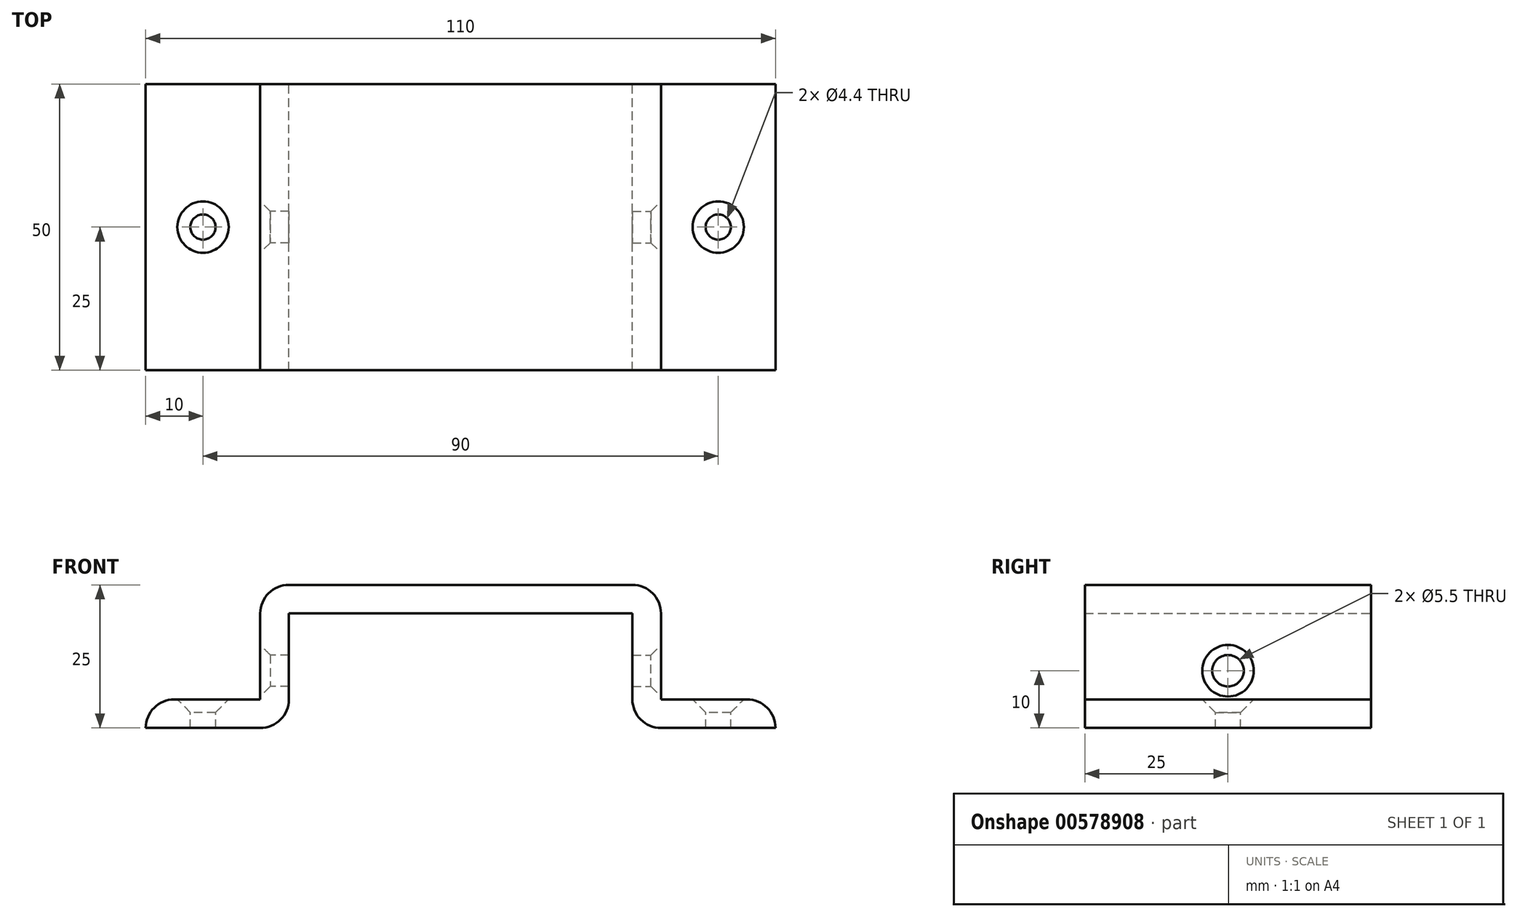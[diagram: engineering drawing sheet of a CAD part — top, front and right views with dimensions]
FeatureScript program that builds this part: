
annotation { "Feature Type Name" : "Feature", "Feature Type Description" : "" }
export const myFeature = defineFeature(function(context is Context, id is Id, definition is map)
    precondition{}
    {
        {
            var Q0;
            Q0=qCreatedBy(makeId("Front.planeOp"),FACE);
            var sketch = newSketch(context, id + "F0", { "sketchPlane" : qUnion([Q0])});
            skLineSegment(sketch, "E0", {"start": v(-55, 0) * mm, "end": v(-30, 0) * mm});
            skLineSegment(sketch, "E1", {"start": v(-30, 0) * mm, "end": v(-30, 20) * mm});
            skLineSegment(sketch, "E2", {"start": v(-30, 20) * mm, "end": v(30, 20) * mm});
            skLineSegment(sketch, "E3", {"start": v(30, 20) * mm, "end": v(30, 0) * mm});
            skLineSegment(sketch, "E4", {"start": v(30, 0) * mm, "end": v(55, 0) * mm});
            skLineSegment(sketch, "E5", {"start": v(-55, 0) * mm, "end": v(-55, 5) * mm});
            skLineSegment(sketch, "E6", {"start": v(-55, 5) * mm, "end": v(-35, 5) * mm});
            skLineSegment(sketch, "E7", {"start": v(-35, 5) * mm, "end": v(-35, 25) * mm});
            skLineSegment(sketch, "E8", {"start": v(-35, 25) * mm, "end": v(35, 25) * mm});
            skLineSegment(sketch, "E9", {"start": v(35, 25) * mm, "end": v(35, 5) * mm});
            skLineSegment(sketch, "E10", {"start": v(35, 5) * mm, "end": v(55, 5) * mm});
            skLineSegment(sketch, "E11", {"start": v(55, 5) * mm, "end": v(55, 0) * mm});
            skLineSegment(sketch, "E12", {"start": v(-30, 0) * mm, "end": v(30, 0) * mm, "construction": true});
            skSolve(sketch);
        }
        {
            var Q0;
            Q0=makeQuery(id+"F0.imprint","IMPRINT",FACE,{"disambiguationData":[TD([[makeQuery(id+"F0.imprint","IMPRINT",EDGE,{"derivedFrom":sQuery(id+"F0.wireOp",EDGE,"E0")}),1.0]])]});
            extrude(context, id + "F1", {"entities" : qUnion([Q0]), "depth" : 50 * mm, "offsetDistance" : 25 * mm});
        }
        {
            var Q0;
            Q0=makeQuery(id+"F1.opExtrude","SWEPT_FACE",FACE,{"disambiguationData":[OSD([sQuery(id+"F0.wireOp",EDGE,"E6")])]});
            var sketch = newSketch(context, id + "F2", { "sketchPlane" : qUnion([Q0])});
            skPoint(sketch, "E13", {"position": v(-45, -25) * mm});
            skLineSegment(sketch, "E14", {"start": v(-35, -25) * mm, "end": v(-55, -25) * mm, "construction": true});
            skLineSegment(sketch, "E15", {"start": v(-45, 0) * mm, "end": v(-45, -50) * mm, "construction": true});
            skSolve(sketch);
        }
        {
            var Q0;
            Q0=makeQuery(id+"F1.opExtrude","SWEPT_FACE",FACE,{"disambiguationData":[OSD([sQuery(id+"F0.wireOp",EDGE,"E10")])]});
            var sketch = newSketch(context, id + "F3", { "sketchPlane" : qUnion([Q0])});
            skLineSegment(sketch, "E16", {"start": v(45, 0) * mm, "end": v(45, -50) * mm, "construction": true});
            skLineSegment(sketch, "E17", {"start": v(55, -25) * mm, "end": v(35, -25) * mm, "construction": true});
            skPoint(sketch, "E18", {"position": v(45, -25) * mm});
            skSolve(sketch);
        }
        {
            var Q0;
            Q0=sQuery(id+"F2.wireOp",VERTEX,"E13");
            var Q1;
            Q1=sQuery(id+"F3.wireOp",VERTEX,"E18");
            var Q2;
            Q2=makeQuery(id+"F1.opExtrude","SWEPT_BODY",BODY,{"disambiguationData":[OSD([sQuery(id+"F0.wireOp",EDGE,"E0"),sQuery(id+"F0.wireOp",EDGE,"E1"),sQuery(id+"F0.wireOp",EDGE,"E2"),sQuery(id+"F0.wireOp",EDGE,"E3"),sQuery(id+"F0.wireOp",EDGE,"E4"),sQuery(id+"F0.wireOp",EDGE,"E5"),sQuery(id+"F0.wireOp",EDGE,"E6"),sQuery(id+"F0.wireOp",EDGE,"E7"),sQuery(id+"F0.wireOp",EDGE,"E8"),sQuery(id+"F0.wireOp",EDGE,"E9"),sQuery(id+"F0.wireOp",EDGE,"E10"),sQuery(id+"F0.wireOp",EDGE,"E11")])]});
            hole(context, id + "F4", {"style" : HoleStyle.C_SINK, "endStyle" : HoleEndStyle.THROUGH, "standardTappedOrClearance" : lookupTablePath({ "standard" : "ISO", "fit" : "Normal", "size" : "M4", "type" : "Clearance" }), "standardBlindInLast" : lookupTablePath({ "fit" : "Standard", "standard" : "ISO", "size" : "M4", "type" : "Clearance" }), "holeDiameter" : 4.4 * mm, "cSinkDiameter" : 8.96 * mm, "cSinkAngle" : 90 * degree, "isTappedThrough" : true, "tappedDepth" : 12 * mm, "tapClearance" : 3, "locations" : qUnion([Q0, Q1]), "scope" : qUnion([Q2]), "majorDiameter" : 5 * mm});
        }
        {
            var Q0;
            Q0=makeQuery(id+"F1.opExtrude","SWEPT_FACE",FACE,{"disambiguationData":[OSD([sQuery(id+"F0.wireOp",EDGE,"E7")])]});
            var sketch = newSketch(context, id + "F5", { "sketchPlane" : qUnion([Q0])});
            skPoint(sketch, "E19", {"position": v(25, 10) * mm});
            skLineSegment(sketch, "E20", {"start": v(25, 5) * mm, "end": v(25, 25) * mm, "construction": true});
            skSolve(sketch);
        }
        {
            var Q0;
            Q0=sQuery(id+"F5.wireOp",VERTEX,"E19");
            var Q1;
            Q1=makeQuery(id+"F1.opExtrude","SWEPT_BODY",BODY,{"disambiguationData":[OSD([sQuery(id+"F0.wireOp",EDGE,"E0"),sQuery(id+"F0.wireOp",EDGE,"E1"),sQuery(id+"F0.wireOp",EDGE,"E2"),sQuery(id+"F0.wireOp",EDGE,"E3"),sQuery(id+"F0.wireOp",EDGE,"E4"),sQuery(id+"F0.wireOp",EDGE,"E5"),sQuery(id+"F0.wireOp",EDGE,"E6"),sQuery(id+"F0.wireOp",EDGE,"E7"),sQuery(id+"F0.wireOp",EDGE,"E8"),sQuery(id+"F0.wireOp",EDGE,"E9"),sQuery(id+"F0.wireOp",EDGE,"E10"),sQuery(id+"F0.wireOp",EDGE,"E11")])]});
            hole(context, id + "F6", {"style" : HoleStyle.C_SINK, "endStyle" : HoleEndStyle.BLIND, "holeDiameter" : 5.5 * mm, "cSinkDiameter" : 9 * mm, "cSinkAngle" : 90 * degree, "majorDiameter" : 5 * mm, "holeDepth" : 5 * mm, "isTappedThrough" : true, "tappedDepth" : 12 * mm, "tapClearance" : 3, "locations" : qUnion([Q0]), "scope" : qUnion([Q1])});
        }
        {
            var Q0;
            Q0=makeQuery(id+"F1.opExtrude","SWEPT_FACE",FACE,{"disambiguationData":[OSD([sQuery(id+"F0.wireOp",EDGE,"E9")])]});
            var sketch = newSketch(context, id + "F7", { "sketchPlane" : qUnion([Q0])});
            skPoint(sketch, "E21", {"position": v(-25, 10) * mm});
            skLineSegment(sketch, "E22", {"start": v(-25, 5) * mm, "end": v(-25, 25) * mm, "construction": true});
            skSolve(sketch);
        }
        {
            var Q0;
            Q0=sQuery(id+"F7.wireOp",VERTEX,"E21");
            var Q1;
            Q1=makeQuery(id+"F1.opExtrude","SWEPT_BODY",BODY,{"disambiguationData":[OSD([sQuery(id+"F0.wireOp",EDGE,"E0"),sQuery(id+"F0.wireOp",EDGE,"E1"),sQuery(id+"F0.wireOp",EDGE,"E2"),sQuery(id+"F0.wireOp",EDGE,"E3"),sQuery(id+"F0.wireOp",EDGE,"E4"),sQuery(id+"F0.wireOp",EDGE,"E5"),sQuery(id+"F0.wireOp",EDGE,"E6"),sQuery(id+"F0.wireOp",EDGE,"E7"),sQuery(id+"F0.wireOp",EDGE,"E8"),sQuery(id+"F0.wireOp",EDGE,"E9"),sQuery(id+"F0.wireOp",EDGE,"E10"),sQuery(id+"F0.wireOp",EDGE,"E11")])]});
            hole(context, id + "F8", {"style" : HoleStyle.C_SINK, "endStyle" : HoleEndStyle.BLIND, "holeDiameter" : 5.5 * mm, "cSinkDiameter" : 9 * mm, "cSinkAngle" : 90 * degree, "majorDiameter" : 5 * mm, "holeDepth" : 5 * mm, "isTappedThrough" : true, "tappedDepth" : 12 * mm, "tapClearance" : 3, "locations" : qUnion([Q0]), "scope" : qUnion([Q1])});
        }
        {
            var Q0;
            Q0=makeQuery(id+"F1.opExtrude","SWEPT_EDGE",EDGE,{"disambiguationData":[OSD([sQuery(id+"F0.wireOp",EDGE,"E0"),sQuery(id+"F0.wireOp",EDGE,"E1")])]});
            var Q1;
            Q1=makeQuery(id+"F1.opExtrude","SWEPT_EDGE",EDGE,{"disambiguationData":[OSD([sQuery(id+"F0.wireOp",EDGE,"E3"),sQuery(id+"F0.wireOp",EDGE,"E4")])]});
            var Q2;
            Q2=makeQuery(id+"F1.opExtrude","SWEPT_EDGE",EDGE,{"disambiguationData":[OSD([sQuery(id+"F0.wireOp",EDGE,"E5"),sQuery(id+"F0.wireOp",EDGE,"E6")])]});
            var Q3;
            Q3=makeQuery(id+"F1.opExtrude","SWEPT_EDGE",EDGE,{"disambiguationData":[OSD([sQuery(id+"F0.wireOp",EDGE,"E10"),sQuery(id+"F0.wireOp",EDGE,"E11")])]});
            var Q4;
            Q4=makeQuery(id+"F1.opExtrude","SWEPT_EDGE",EDGE,{"disambiguationData":[OSD([sQuery(id+"F0.wireOp",EDGE,"E7"),sQuery(id+"F0.wireOp",EDGE,"E8")])]});
            var Q5;
            Q5=makeQuery(id+"F1.opExtrude","SWEPT_EDGE",EDGE,{"disambiguationData":[OSD([sQuery(id+"F0.wireOp",EDGE,"E8"),sQuery(id+"F0.wireOp",EDGE,"E9")])]});
            fillet(context, id + "F9", {"entities" : qUnion([Q0, Q1, Q2, Q3, Q4, Q5]), "radius" : 5 * mm, "tangentPropagation" : true, "allowEdgeOverflow" : false});
        }
    });
